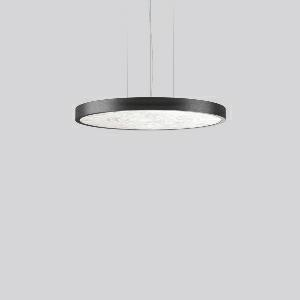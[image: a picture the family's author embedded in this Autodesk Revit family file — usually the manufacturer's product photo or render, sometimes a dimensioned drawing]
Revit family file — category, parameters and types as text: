
# Revit family: triona_round_p_312293_0031_1_76_a3eb
name_source: partatom
category: Lighting Fixtures
units: mm (PartAtom-declared; Revit-internal decimal feet)

## family parameters
Cut with Voids When Loaded = No
Host = Face
Light Source = No
Part Type = Normal
Room Calculation Point = No
Round Connector Dimension = Use Diameter
Shared = No

## types (1)
- TRIONA round P (1 x LED Modul 840, 6350 lm, 4000)
    Apparent Load = 64 VA
    CIE Flux Codes = 48 80 96 76 100
    Color Rendering = 80
    Color Temperature = 4000
    Default Elevation = 1800 mm
    Description = Series: TRIONA round
Decorative round LED pendant-mounted surface luminaire. Flat, seamless frame: aluminium extrusion profile, powder coated. Cover made of sheet steel, powder-coated. Canopy made of aluminium, powder-coated. Direct light emission through a diffuser made of handmade white Ferro Murano coloured glass. Indirect light emission through a flush diffuser made of satin-finish plastic. Lightguide and diffuser made of non-yellowing plastic (PMMA). Lateral light emission (RZB SIDELITE technology) for above-average homogeneous light distribution. Direct 70%, indirect 30% light emission. 3-point steel cable suspension, steplessly adjustable. Easy installation with transparent, adjustable pendant cable and canopy with magnetic fixing. Driver integrated. 
Colour: anthracite metallic (DB703)
Diameter: 681 mm
Height: 52 mm
Suspension length: 500-1200 mm
Lamp: LED
Socket: without socket
Colour temperature: 4000K
Colour rendering index (CRI): 80
System power: 64 W
Rated luminous flux: 6350 lm
Luminous efficiency: 99 lm/W
Control gear: Converter, dimmable, DALI
Protection class: I
Type of protection: IP 20
    Height = 52 mm  [stored 0.170604 ft]
    Lamp = 1 x LED Modul 840
    Lamp Light Flux = 6350 lm
    Lamp count = 1
    Length = 681 mm
    Lifetime = 50000 h
    Luminous efficacy = 99 lm/W
    Manufacturer = RZB
    ModVariant = No
    Model = 312293.0031.1.76
    Mounting Place = Ceiling
    Mounting Type = Pendant
    Number of Poles = 1
    OnlyDefault = Yes
    Power Factor = 1
    Product Name = TRIONA round P
    Product group = Pendant modular luminaires
    ProductGroupID = 906
    Protection Class = Protection class I
    Protection Degree = IP 20
    RLX_Detail_Level = 1
    RLX_Emergency_Light_Flux = 0 lm
    RLX_Emergency_Type = 0
    RLX_Emergency_Type_DB = No
    RlxData = <blob elided: 40313 chars, md5=2d7f1568>
    Socket = socket
    Standby Power = 0 W
    System Light Flux = 6356 lm
    System Power = 64 W
    Type Comments = Product without accessories
    Type Image = 312293.0031.jpg
    URL = http://relux.com
    VarID = ---
    Voltage = 230 V
    Voltage Range = 220-240 V
    Weight = 0.00 kg
    Width = 0 mm  [stored 0 ft]

note: [stored X ft] marks values corroborated as IEEE doubles in the binary element streams (Revit-internal decimal feet)

## geometry (parser evidence)
native form markers: Blend x4, Sweep x14
no freeform markers — native parametric forms only
